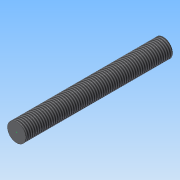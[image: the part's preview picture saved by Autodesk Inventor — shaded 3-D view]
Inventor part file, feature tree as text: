
AUTODESK INVENTOR PART (.ipt)
format: ipt  version: 2015 (Build 190159000, 159)  size: 83,456 bytes
history: native  units: mm
features: sketch x3, extrude x1, thread x1
ambient origin geometry x8: Origin, YZ Plane, XZ Plane, XY Plane, X Axis, Y Axis, Z Axis, Center Point
bodies: Solid1 (feature_tree)
feature tree (5):
  sketch  "Sketch1"  dims[d0=10.0mm d1=80.0mm d2=0.0mm d3=10.0mm d4=0.0mm]
  sketch  "Sketch2"
  extrude  "Extrusion1"  Depth=80.0mm TaperAngle=0.0deg
  thread  "Thread1"  [1 undecoded]
  sketch  "Sketch3"
note: 1 required parameter value undecoded (feature->parameter linkage not recoverable at this tier; creation-order binding heuristic only, values carry confidence <= 0.55)
